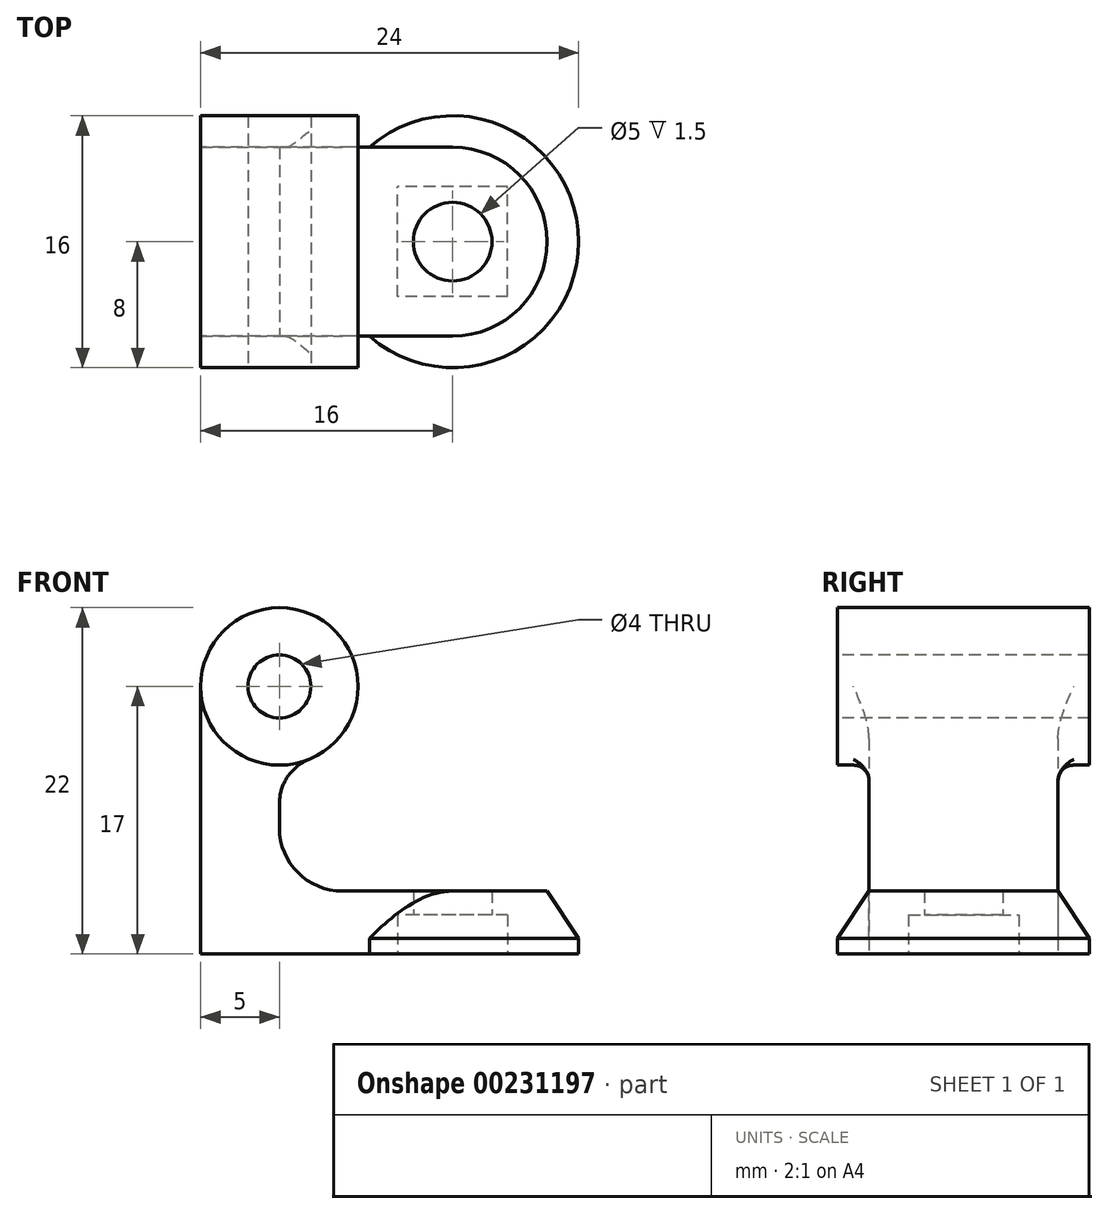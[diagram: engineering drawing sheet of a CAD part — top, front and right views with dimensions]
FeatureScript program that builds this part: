
annotation { "Feature Type Name" : "Feature", "Feature Type Description" : "" }
export const myFeature = defineFeature(function(context is Context, id is Id, definition is map)
    precondition{}
    {
        {
            var Q0;
            Q0=qCreatedBy(makeId("Top.planeOp"),FACE);
            var sketch = newSketch(context, id + "F0", { "sketchPlane" : qUnion([Q0])});
            skLineSegment(sketch, "E0.bottom", {"start": v(12, 6) * mm, "end": v(-12, 6) * mm});
            skLineSegment(sketch, "E0.top", {"start": v(12, -6) * mm, "end": v(-12, -6) * mm});
            skLineSegment(sketch, "E0.left", {"start": v(12, 6) * mm, "end": v(12, -6) * mm});
            skLineSegment(sketch, "E0.right", {"start": v(-12, 6) * mm, "end": v(-12, -6) * mm});
            skPoint(sketch, "E0.middle", {"position": v(0, 0) * mm});
            skCircle(sketch, "E1", {"center": v(4, 0) * mm, "radius": 8 * mm});
            skCircle(sketch, "E2", {"center": v(4, 0) * mm, "radius": 2.5 * mm});
            skLineSegment(sketch, "E3.bottom", {"start": v(7.5, 3.5) * mm, "end": v(0.5, 3.5) * mm});
            skLineSegment(sketch, "E3.top", {"start": v(7.5, -3.5) * mm, "end": v(0.5, -3.5) * mm});
            skLineSegment(sketch, "E3.left", {"start": v(7.5, -3.5) * mm, "end": v(7.5, 3.5) * mm});
            skLineSegment(sketch, "E3.right", {"start": v(0.5, -3.5) * mm, "end": v(0.5, 3.5) * mm});
            skLineSegment(sketch, "E4", {"start": v(-7, -6) * mm, "end": v(-7, 6) * mm});
            skSolve(sketch);
        }
        {
            var Q0;
            {var subQ0=sQuery(id+"F0.wireOp",EDGE,"E0.right");Q0=makeQuery(id+"F0.imprint","IMPRINT",FACE,{"disambiguationData":[TD([[makeQuery(id+"F0.imprint","IMPRINT",EDGE,{"derivedFrom":subQ0}),1.0]])]});}
            var Q1;
            Q1=makeQuery(id+"F0.imprint","IMPRINT",FACE,{"disambiguationData":[TD([[makeQuery(id+"F0.imprint","IMPRINT",EDGE,{"derivedFrom":sQuery(id+"F0.wireOp",EDGE,"E3.bottom")}),-1.0]])]});
            var Q2;
            {var subQ0=sQuery(id+"F0.wireOp",EDGE,"E1");var subQ1=sQuery(id+"F0.wireOp",EDGE,"E0.top");var subQ2=makeQuery(id+"F0.imprint","INTERSECT",VERTEX,{"disambiguationData":[OD(0.0)],"derivedFrom":[subQ1,subQ0]});Q2=makeQuery(id+"F0.imprint","IMPRINT",FACE,{"disambiguationData":[TD([[makeQuery(id+"F0.imprint","IMPRINT",EDGE,{"disambiguationData":[TD([[subQ2,-1.0]])],"derivedFrom":subQ1}),1.0]])]});}
            var Q3;
            {var subQ0=sQuery(id+"F0.wireOp",EDGE,"E1");var subQ1=sQuery(id+"F0.wireOp",EDGE,"E0.bottom");var subQ2=makeQuery(id+"F0.imprint","INTERSECT",VERTEX,{"disambiguationData":[OD(0.0)],"derivedFrom":[subQ1,subQ0]});Q3=makeQuery(id+"F0.imprint","IMPRINT",FACE,{"disambiguationData":[TD([[makeQuery(id+"F0.imprint","IMPRINT",EDGE,{"disambiguationData":[TD([[subQ2,-1.0]])],"derivedFrom":subQ1}),-1.0]])]});}
            extrude(context, id + "F1", {"entities" : qUnion([Q0, Q1, Q2, Q3]), "depth" : 4 * mm});
        }
        {
            var Q0;
            Q0=makeQuery(id+"F0.imprint","IMPRINT",FACE,{"disambiguationData":[TD([[makeQuery(id+"F0.imprint","IMPRINT",EDGE,{"derivedFrom":sQuery(id+"F0.wireOp",EDGE,"E2")}),-1.0]])]});
            extrude(context, id + "F2", {"entities" : qUnion([Q0]), "operationType" : NewBodyOperationType.ADD, "depth" : 4 * mm, "hasSecondDirection" : true, "secondDirectionOppositeDirection" : false, "secondDirectionDepth" : 2.5 * mm});
        }
        {
            var Q0;
            Q0=makeQuery(id+"F1.opExtrude","SWEPT_BODY",BODY,{"disambiguationData":[OSD([sQuery(id+"F0.wireOp",EDGE,"E0.bottom"),sQuery(id+"F0.wireOp",EDGE,"E0.top"),sQuery(id+"F0.wireOp",EDGE,"E0.right"),sQuery(id+"F0.wireOp",EDGE,"E4")])]});
            deleteBodies(context, id + "F3", {"entities" : qUnion([Q0])});
        }
        {
            var Q0;
            {var subQ0=sQuery(id+"F0.wireOp",EDGE,"E0.right");Q0=makeQuery(id+"F0.imprint","IMPRINT",FACE,{"disambiguationData":[TD([[makeQuery(id+"F0.imprint","IMPRINT",EDGE,{"derivedFrom":subQ0}),1.0]])]});}
            var Q1;
            {var subQ0=sQuery(id+"F0.wireOp",EDGE,"E4");Q1=makeQuery(id+"F0.imprint","IMPRINT",FACE,{"disambiguationData":[TD([[makeQuery(id+"F0.imprint","IMPRINT",EDGE,{"derivedFrom":subQ0}),-1.0]])]});}
            extrude(context, id + "F4", {"entities" : qUnion([Q0, Q1]), "operationType" : NewBodyOperationType.ADD, "depth" : 4 * mm});
        }
        {
            var Q0;
            {var subQ0=sQuery(id+"F0.wireOp",EDGE,"E0.right");Q0=makeQuery(id+"F0.imprint","IMPRINT",FACE,{"disambiguationData":[TD([[makeQuery(id+"F0.imprint","IMPRINT",EDGE,{"derivedFrom":subQ0}),1.0]])]});}
            extrude(context, id + "F5", {"entities" : qUnion([Q0]), "operationType" : NewBodyOperationType.ADD, "depth" : 17 * mm});
        }
        {
            var Q0;
            Q0=makeQuery(id+"F1.opExtrude","CAP_EDGE",EDGE,{"disambiguationData":[OSD([sQuery(id+"F0.wireOp",EDGE,"E1")])],"isStart":false});
            chamfer(context, id + "F6", {"entities" : qUnion([Q0]), "chamferType" : ChamferType.TWO_OFFSETS, "width1" : 2 * mm, "oppositeDirection" : false, "width2" : 3 * mm, "tangentPropagation" : true});
        }
        {
            var Q0;
            Q0=qCreatedBy(makeId("Front.planeOp"),FACE);
            var sketch = newSketch(context, id + "F7", { "sketchPlane" : qUnion([Q0])});
            skCircle(sketch, "E5", {"center": v(-7, 17) * mm, "radius": 5 * mm});
            skCircle(sketch, "E6", {"center": v(-7, 17) * mm, "radius": 2 * mm});
            skSolve(sketch);
        }
        {
            var Q0;
            Q0=makeQuery(id+"F7.imprint","IMPRINT",FACE,{"disambiguationData":[TD([[makeQuery(id+"F7.imprint","IMPRINT",EDGE,{"derivedFrom":sQuery(id+"F7.wireOp",EDGE,"E6")}),1.0]])]});
            extrude(context, id + "F8", {"entities" : qUnion([Q0]), "operationType" : NewBodyOperationType.REMOVE, "oppositeDirection" : true, "depth" : 25 * mm, "hasSecondDirection" : true, "secondDirectionOppositeDirection" : false, "secondDirectionDepth" : 25 * mm});
        }
        {
            var Q0;
            {var subQ0=sQuery(id+"F0.wireOp",EDGE,"E1");var subQ1=sQuery(id+"F0.wireOp",EDGE,"E3.right");var subQ2=sQuery(id+"F0.wireOp",EDGE,"E3.left");var subQ3=sQuery(id+"F0.wireOp",EDGE,"E3.top");var subQ4=sQuery(id+"F0.wireOp",EDGE,"E3.bottom");Q0=makeQuery(id+"F5.boolean.opBoolean","INTERSECT",EDGE,{"derivedFrom":[makeQuery(id+"F4.boolean.opBoolean","MERGE",FACE,{"derivedFrom":[makeQuery(id+"F2.boolean.opBoolean","MERGE",FACE,{"derivedFrom":[makeQuery(id+"F1.opExtrude","CAP_FACE",FACE,{"disambiguationData":[OSD([subQ0,subQ4,subQ3,subQ2,subQ1])],"isStart":false}),makeQuery(id+"F2.opExtrude","CAP_FACE",FACE,{"disambiguationData":[OSD([sQuery(id+"F0.wireOp",EDGE,"E2"),subQ4,subQ3,subQ2,subQ1])],"isStart":false})]}),makeQuery(id+"F4.opExtrude","CAP_FACE",FACE,{"disambiguationData":[OSD([sQuery(id+"F0.wireOp",EDGE,"E0.bottom"),sQuery(id+"F0.wireOp",EDGE,"E0.top"),sQuery(id+"F0.wireOp",EDGE,"E0.right"),subQ0])],"isStart":false})]}),makeQuery(id+"F5.opExtrude","SWEPT_FACE",FACE,{"disambiguationData":[OSD([sQuery(id+"F0.wireOp",EDGE,"E4")])]})]});}
            fillet(context, id + "F9", {"entities" : qUnion([Q0]), "tangentPropagation" : true, "radius" : 4 * mm, "defaultsChanged" : true, "vertexSettings" : [], "allowEdgeOverflow" : false});
        }
        {
            var Q0;
            Q0=qSketchRegion(id+"F7",true);
            extrude(context, id + "F10", {"entities" : qUnion([Q0]), "operationType" : NewBodyOperationType.ADD, "endBound" : BoundingType.SYMMETRIC, "depth" : 16 * mm, "offsetDistance" : 25 * mm});
        }
        {
            var Q0;
            Q0=makeQuery(id+"F10.boolean.opBoolean","INTERSECT",EDGE,{"derivedFrom":[makeQuery(id+"F5.opExtrude","SWEPT_FACE",FACE,{"disambiguationData":[OSD([sQuery(id+"F0.wireOp",EDGE,"E4")])]}),makeQuery(id+"F10.opExtrude","SWEPT_FACE",FACE,{"disambiguationData":[OSD([sQuery(id+"F7.wireOp",EDGE,"E5")])]})]});
            fillet(context, id + "F11", {"entities" : qUnion([Q0]), "tangentPropagation" : true, "radius" : 3 * mm, "defaultsChanged" : true, "vertexSettings" : [], "allowEdgeOverflow" : false});
        }
        {
            var Q0;
            {var subQ0=sQuery(id+"F0.wireOp",EDGE,"E0.top");Q0=makeQuery(id+"F10.boolean.opBoolean","INTERSECT",EDGE,{"derivedFrom":[makeQuery(id+"F5.boolean.opBoolean","MERGE",FACE,{"derivedFrom":[makeQuery(id+"F4.opExtrude","SWEPT_FACE",FACE,{"disambiguationData":[OSD([subQ0])]}),makeQuery(id+"F5.opExtrude","SWEPT_FACE",FACE,{"disambiguationData":[OSD([subQ0])]})]}),makeQuery(id+"F10.opExtrude","SWEPT_FACE",FACE,{"disambiguationData":[OSD([sQuery(id+"F7.wireOp",EDGE,"E5")])]})]});}
            var Q1;
            {var subQ0=sQuery(id+"F0.wireOp",EDGE,"E0.bottom");Q1=makeQuery(id+"F10.boolean.opBoolean","INTERSECT",EDGE,{"derivedFrom":[makeQuery(id+"F5.boolean.opBoolean","MERGE",FACE,{"derivedFrom":[makeQuery(id+"F4.opExtrude","SWEPT_FACE",FACE,{"disambiguationData":[OSD([subQ0])]}),makeQuery(id+"F5.opExtrude","SWEPT_FACE",FACE,{"disambiguationData":[OSD([subQ0])]})]}),makeQuery(id+"F10.opExtrude","SWEPT_FACE",FACE,{"disambiguationData":[OSD([sQuery(id+"F7.wireOp",EDGE,"E5")])]})]});}
            fillet(context, id + "F12", {"entities" : qUnion([Q0, Q1]), "tangentPropagation" : true, "radius" : 1 * mm, "defaultsChanged" : false, "vertexSettings" : [], "allowEdgeOverflow" : false});
        }
    });
